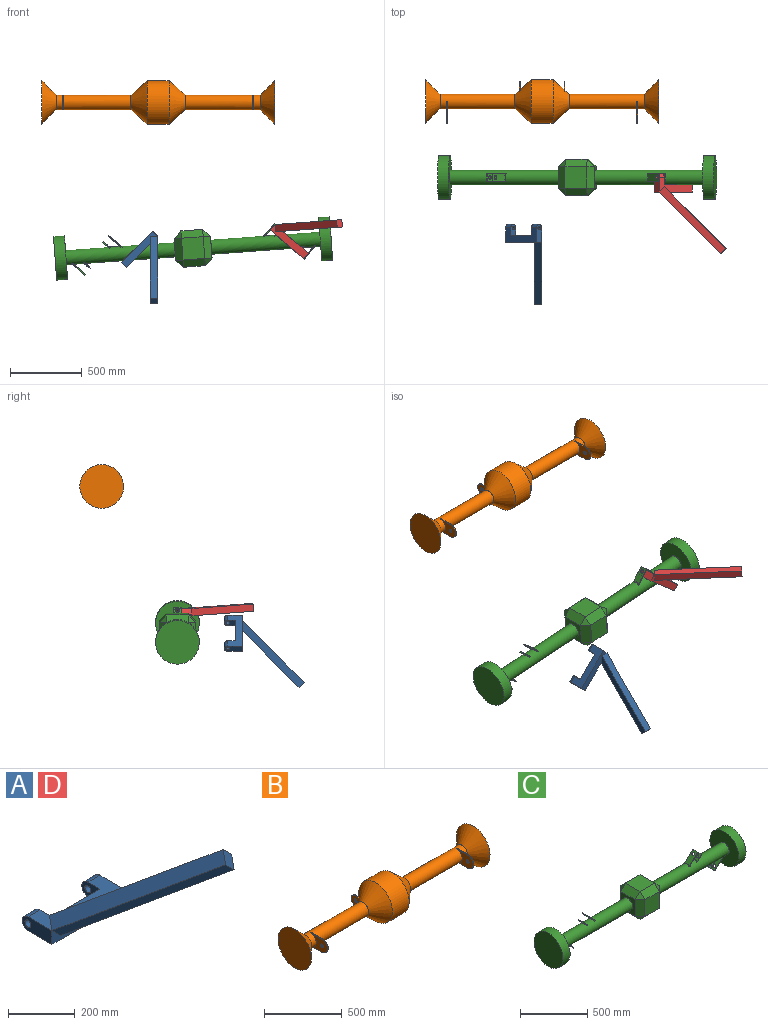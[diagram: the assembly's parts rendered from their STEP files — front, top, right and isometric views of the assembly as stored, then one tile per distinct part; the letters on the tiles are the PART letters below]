
ASSEMBLY  parts=4 mates=1
PART A: 18 faces, bbox 366.1x558.1x381 mm
  f0: plane 76.2x50.8mm, normal (-1,0,0), area 3087.3mm2, adj f2,f3,f4,f5,f6
  f1: plane 127x50.8mm, normal (1,0,0), area 5668mm2, adj f2,f3,f4,f5,f11
  f2: cylinder r=25.4mm len=50.8mm, axis (1,0,0), area 4053.7mm2, adj f0,f1,f3,f4
  f3: plane 304.8x101.6mm, normal (0,0,1), area 19133.4mm2, adj f0,f1,f2,f6,f7,f8,f9,f11
  f4: plane 304.8x101.6mm, normal (0,0,-1), area 20645.1mm2, adj f0,f1,f2,f6,f7,f8,f9,f11
  f5: cylinder r=12.7mm len=50.8mm, axis (1,0,0), area 4053.7mm2, adj f0,f1
  f6: plane 203.2x50.8mm, normal (0,1,0), area 10322.6mm2, adj f0,f3,f4,f7
  f7: plane 76.2x50.8mm, normal (1,0,0), area 3087.3mm2, adj f3,f4,f6,f9,f10
  f8: plane 127x50.8mm, normal (-1,0,0), area 5668mm2, adj f3,f4,f9,f10,f11
  f9: cylinder r=25.4mm len=50.8mm, axis (-1,0,0), area 4053.7mm2, adj f3,f4,f7,f8
  f10: cylinder r=12.7mm len=50.8mm, axis (-1,0,0), area 4053.7mm2, adj f7,f8
  f11: plane 304.8x50.8mm, normal (0,-1,0), area 14193.5mm2, adj f1,f3,f4,f8,f12,f16
  f12: plane 431.05x340.72mm, normal (-0.5,-0.71,-0.5), area 30967.7mm2, adj f11,f15,f16,f17
  f13: plane 50.8x35.92mm, normal (-0.5,0.71,-0.5), area 912.4mm2, adj f3,f14,f17
  f14: plane 431.05x340.72mm, normal (0.5,0.71,0.5), area 30811.1mm2, adj f3,f13,f15,f16,f17
  f15: plane 61.32x61.32mm, normal (0.5,-0.71,0.5), area 2580.6mm2, adj f12,f14,f16,f17
  f16: plane 452.09x330.2mm, normal (0.71,0,-0.71), area 29898.7mm2, adj f3,f11,f12,f14,f15
  f17: plane 466.97x330.2mm, normal (-0.71,0,0.71), area 30967.7mm2, adj f12,f13,f14,f15
PART B: 38 faces, bbox 1625.7x304.9x304.9 mm
  f0: plane 304.8x304.8mm, normal (1,0,0), area 62643.3mm2, adj f1,f15,f16,f17,f18
  f1: cone r=152.4mm half-angle=45deg, axis (1,0,0), area 91723.9mm2, adj f0,f2
  f2: cylinder r=50.8mm len=521.41mm, axis (1,0,0), area 165412.5mm2, adj f1,f3,f26,f29,f30,f31
  f3: cone r=50.8mm half-angle=41.8deg, axis (-1,0,0), area 96611.5mm2, adj f2,f4,f9,f10,f13,f14
  f4: cylinder r=152.4mm len=304.8mm, axis (1,0,0), area 145931.8mm2, adj f3,f5
  f5: cone r=50.8mm half-angle=41.8deg, axis (1,0,0), area 96611.5mm2, adj f4,f6,f20,f21,f24,f25
  f6: cylinder r=50.8mm len=521.41mm, axis (1,0,0), area 165412.5mm2, adj f5,f7,f32,f35,f36,f37
  f7: cone r=152.4mm half-angle=45deg, axis (-1,0,0), area 91723.9mm2, adj f6,f8
  f8: plane 304.8x304.8mm, normal (-1,0,0), area 72965.9mm2, adj f7
  f9: plane 33.01x6.47mm, normal (0,0,1), area 188.4mm2, adj f3,f11,f13,f14
  f10: plane 33.01x6.47mm, normal (0,0,-1), area 188.4mm2, adj f3,f11,f13,f14
  f11: cylinder r=38.1mm len=76.2mm, axis (-1,0,0), area 760.1mm2, adj f9,f10,f13,f14
  f12: cylinder r=12.7mm len=25.4mm, axis (-1,0,0), area 506.7mm2, adj f13,f14
  f13: plane 76.2x70.99mm, normal (1,0,0), area 3772.5mm2, adj f3,f9,f10,f11,f12
  f14: plane 76.2x64.56mm, normal (-1,0,0), area 3322mm2, adj f3,f9,f10,f11,f12
  f15: plane 203.2x6.35mm, normal (0,1,0), area 1290.3mm2, adj f0,f16,f18,f19
  f16: plane 50.8x6.35mm, normal (0,0,1), area 322.6mm2, adj f0,f15,f17,f19
  f17: plane 203.2x6.35mm, normal (0,-1,0), area 1290.3mm2, adj f0,f16,f18,f19
  f18: plane 50.8x6.35mm, normal (0,0,-1), area 322.6mm2, adj f0,f15,f17,f19
  f19: plane 203.2x50.8mm, normal (1,0,0), area 10322.6mm2, adj f15,f16,f17,f18
  f20: plane 33.01x6.47mm, normal (0,0,1), area 188.4mm2, adj f5,f22,f24,f25
  f21: plane 33.01x6.47mm, normal (0,0,-1), area 188.4mm2, adj f5,f22,f24,f25
  f22: cylinder r=38.1mm len=76.2mm, axis (1,0,0), area 760.1mm2, adj f20,f21,f24,f25
  f23: cylinder r=12.7mm len=25.4mm, axis (1,0,0), area 506.7mm2, adj f24,f25
  f24: plane 76.2x70.99mm, normal (-1,0,0), area 3772.5mm2, adj f5,f20,f21,f22,f23
  f25: plane 76.2x64.56mm, normal (1,0,0), area 3322mm2, adj f5,f20,f21,f22,f23
  f26: plane 101.6x6.35mm, normal (0,0,1), area 645.2mm2, adj f2,f27,f30,f31
  f27: cylinder r=50.8mm len=101.6mm, axis (-1,0,0), area 1013.4mm2, adj f26,f29,f30,f31
  f28: cylinder r=12.7mm len=25.4mm, axis (-1,0,0), area 506.7mm2, adj f30,f31
  f29: plane 101.6x6.35mm, normal (0,0,-1), area 645.2mm2, adj f2,f27,f30,f31
  f30: plane 152.4x101.6mm, normal (1,0,0), area 9815.9mm2, adj f2,f26,f27,f28,f29
  f31: plane 152.4x101.6mm, normal (-1,0,0), area 9815.9mm2, adj f2,f26,f27,f28,f29
  f32: plane 101.6x6.35mm, normal (0,0,-1), area 645.2mm2, adj f6,f33,f36,f37
  f33: cylinder r=50.8mm len=101.6mm, axis (1,0,0), area 1013.4mm2, adj f32,f35,f36,f37
  f34: cylinder r=12.7mm len=25.4mm, axis (1,0,0), area 506.7mm2, adj f36,f37
  f35: plane 101.6x6.35mm, normal (0,0,1), area 645.2mm2, adj f6,f33,f36,f37
  f36: plane 152.4x101.6mm, normal (-1,0,0), area 9815.9mm2, adj f6,f32,f33,f34,f35
  f37: plane 152.4x101.6mm, normal (1,0,0), area 9815.9mm2, adj f6,f32,f33,f34,f35
PART C: 82 faces, bbox 1930.4x304.8x304.8 mm
  f0: plane 152.4x152.4mm, normal (0,0,-1), area 23225.8mm2, adj f9,f13,f14,f52
  f1: plane 152.4x152.4mm, normal (0,1,0), area 23225.8mm2, adj f9,f11,f12,f51
  f2: plane 152.4x152.4mm, normal (0,0,1), area 23225.8mm2, adj f11,f17,f20,f55
  f3: plane 152.4x152.4mm, normal (0,-1,0), area 23225.8mm2, adj f14,f18,f20,f56
  f4: plane 152.4x152.4mm, normal (1,0,0), area 15118.4mm2, adj f5,f12,f13,f17,f18
  f5: cylinder r=50.8mm len=762mm, axis (-1,0,0), area 241308.7mm2, adj f4,f8,f21,f22,f23,f25,f26,f27
  f6: cylinder r=152.4mm len=304.8mm, axis (-1,0,0), area 72965.9mm2, adj f7,f8
  f7: plane 304.8x304.8mm, normal (1,0,0), area 72965.9mm2, adj f6
  f8: plane 304.8x304.8mm, normal (-1,0,0), area 64858.6mm2, adj f5,f6
  f9: plane 152.4x50.8mm, normal (0,0.71,-0.71), area 10948.7mm2, adj f0,f1,f10,f50
  f10: plane 50.8x50.8mm, normal (0.58,0.58,-0.58), area 2234.9mm2, adj f9,f12,f13
  f11: plane 152.4x50.8mm, normal (0,0.71,0.71), area 10948.7mm2, adj f1,f2,f15,f53
  f12: plane 152.4x50.8mm, normal (0.71,0.71,0), area 10948.7mm2, adj f1,f4,f10,f15
  f13: plane 152.4x50.8mm, normal (0.71,0,-0.71), area 10948.7mm2, adj f0,f4,f10,f16
  f14: plane 152.4x50.8mm, normal (0,-0.71,-0.71), area 10948.7mm2, adj f0,f3,f16,f54
  f15: plane 50.8x50.8mm, normal (0.58,0.58,0.58), area 2234.9mm2, adj f11,f12,f17
  f16: plane 50.8x50.8mm, normal (0.58,-0.58,-0.58), area 2234.9mm2, adj f13,f14,f18
  f17: plane 152.4x50.8mm, normal (0.71,0,0.71), area 10948.7mm2, adj f2,f4,f15,f19
  f18: plane 152.4x50.8mm, normal (0.71,-0.71,0), area 10948.7mm2, adj f3,f4,f16,f19
  f19: plane 50.8x50.8mm, normal (0.58,-0.58,0.58), area 2234.9mm2, adj f17,f18,f20
  f20: plane 152.4x50.8mm, normal (0,-0.71,0.71), area 10948.7mm2, adj f2,f3,f19,f57
  f21: plane 51.71x47.22mm, normal (0,-1,0), area 403.9mm2, adj f5,f23,f24,f25
  f22: plane 51.71x47.22mm, normal (0,1,0), area 403.9mm2, adj f5,f23,f24,f25
  f23: plane 50.8x42.73mm, normal (-0.71,0,0.71), area 2232.3mm2, adj f5,f21,f22,f24,f44
  f24: plane 50.8x4.49mm, normal (-0.71,0,-0.71), area 322.6mm2, adj f21,f22,f23,f25
  f25: plane 50.8x47.22mm, normal (0.71,0,-0.71), area 2554.9mm2, adj f5,f21,f22,f24,f44
  f26: plane 92.12x87.63mm, normal (0,-1,0), area 766.8mm2, adj f5,f28,f29,f30
  f27: plane 92.12x87.63mm, normal (0,1,0), area 766.8mm2, adj f5,f28,f29,f30
  f28: plane 83.14x83.14mm, normal (-0.71,0,0.71), area 5135.5mm2, adj f5,f26,f27,f29,f43
  f29: plane 50.8x4.49mm, normal (-0.71,0,-0.71), area 322.6mm2, adj f26,f27,f28,f30
  f30: plane 87.63x87.63mm, normal (0.71,0,-0.71), area 5458.1mm2, adj f5,f26,f27,f29,f43
  f31: plane 92.12x87.63mm, normal (0,-1,0), area 766.8mm2, adj f5,f33,f34,f35
  f32: plane 92.12x87.63mm, normal (0,1,0), area 766.8mm2, adj f5,f33,f34,f35
  f33: plane 87.63x87.63mm, normal (-0.71,0,0.71), area 5458.1mm2, adj f5,f31,f32,f35,f42
  f34: plane 83.14x83.14mm, normal (0.71,0,-0.71), area 5135.5mm2, adj f5,f31,f32,f35,f42
  f35: plane 50.8x4.49mm, normal (0.71,0,0.71), area 322.6mm2, adj f31,f32,f33,f34
  f36: plane 51.71x47.22mm, normal (0,-1,0), area 403.9mm2, adj f5,f38,f39,f40
  f37: plane 51.71x47.22mm, normal (0,1,0), area 403.9mm2, adj f5,f38,f39,f40
  f38: plane 50.8x42.73mm, normal (0.71,0,-0.71), area 2232.3mm2, adj f5,f36,f37,f39,f41
  f39: plane 50.8x4.49mm, normal (0.71,0,0.71), area 322.6mm2, adj f36,f37,f38,f40
  f40: plane 50.8x47.22mm, normal (-0.71,0,0.71), area 2554.9mm2, adj f5,f36,f37,f39,f41
  f41: cylinder r=12.7mm len=25.4mm, axis (-0.71,0,0.71), area 506.7mm2, adj f38,f40
  f42: cylinder r=12.7mm len=25.4mm, axis (-0.71,0,0.71), area 506.7mm2, adj f33,f34
  f43: cylinder r=12.7mm len=25.4mm, axis (0.71,0,-0.71), area 506.7mm2, adj f28,f30
  f44: cylinder r=12.7mm len=25.4mm, axis (0.71,0,-0.71), area 506.7mm2, adj f23,f25
  f45: plane 152.4x152.4mm, normal (-1,0,0), area 15118.4mm2, adj f46,f51,f52,f55,f56
  f46: cylinder r=50.8mm len=762mm, axis (1,0,0), area 241308.7mm2, adj f45,f49,f58,f59,f60,f62,f63,f64
  f47: cylinder r=152.4mm len=304.8mm, axis (1,0,0), area 72965.9mm2, adj f48,f49
  f48: plane 304.8x304.8mm, normal (-1,0,0), area 72965.9mm2, adj f47
  f49: plane 304.8x304.8mm, normal (1,0,0), area 64858.6mm2, adj f46,f47
  f50: plane 50.8x50.8mm, normal (-0.58,0.58,-0.58), area 2234.9mm2, adj f9,f51,f52
  f51: plane 152.4x50.8mm, normal (-0.71,0.71,0), area 10948.7mm2, adj f1,f45,f50,f53
  f52: plane 152.4x50.8mm, normal (-0.71,0,-0.71), area 10948.7mm2, adj f0,f45,f50,f54
  f53: plane 50.8x50.8mm, normal (-0.58,0.58,0.58), area 2234.9mm2, adj f11,f51,f55
  f54: plane 50.8x50.8mm, normal (-0.58,-0.58,-0.58), area 2234.9mm2, adj f14,f52,f56
  f55: plane 152.4x50.8mm, normal (-0.71,0,0.71), area 10948.7mm2, adj f2,f45,f53,f57
  f56: plane 152.4x50.8mm, normal (-0.71,-0.71,0), area 10948.7mm2, adj f3,f45,f54,f57
  f57: plane 50.8x50.8mm, normal (-0.58,-0.58,0.58), area 2234.9mm2, adj f20,f55,f56
  f58: plane 51.71x47.22mm, normal (0,-1,0), area 403.9mm2, adj f46,f60,f61,f62
  f59: plane 51.71x47.22mm, normal (0,1,0), area 403.9mm2, adj f46,f60,f61,f62
  f60: plane 50.8x42.73mm, normal (0.71,0,0.71), area 2232.3mm2, adj f46,f58,f59,f61,f81
  f61: plane 50.8x4.49mm, normal (0.71,0,-0.71), area 322.6mm2, adj f58,f59,f60,f62
  f62: plane 50.8x47.22mm, normal (-0.71,0,-0.71), area 2554.9mm2, adj f46,f58,f59,f61,f81
  f63: plane 92.12x87.63mm, normal (0,-1,0), area 766.8mm2, adj f46,f65,f66,f67
  f64: plane 92.12x87.63mm, normal (0,1,0), area 766.8mm2, adj f46,f65,f66,f67
  f65: plane 83.14x83.14mm, normal (0.71,0,0.71), area 5135.5mm2, adj f46,f63,f64,f66,f80
  f66: plane 50.8x4.49mm, normal (0.71,0,-0.71), area 322.6mm2, adj f63,f64,f65,f67
  f67: plane 87.63x87.63mm, normal (-0.71,0,-0.71), area 5458.1mm2, adj f46,f63,f64,f66,f80
  f68: plane 92.12x87.63mm, normal (0,-1,0), area 766.8mm2, adj f46,f70,f71,f72
  f69: plane 92.12x87.63mm, normal (0,1,0), area 766.8mm2, adj f46,f70,f71,f72
  f70: plane 87.63x87.63mm, normal (0.71,0,0.71), area 5458.1mm2, adj f46,f68,f69,f72,f79
  f71: plane 83.14x83.14mm, normal (-0.71,0,-0.71), area 5135.5mm2, adj f46,f68,f69,f72,f79
  f72: plane 50.8x4.49mm, normal (-0.71,0,0.71), area 322.6mm2, adj f68,f69,f70,f71
  f73: plane 51.71x47.22mm, normal (0,-1,0), area 403.9mm2, adj f46,f75,f76,f77
  f74: plane 51.71x47.22mm, normal (0,1,0), area 403.9mm2, adj f46,f75,f76,f77
  f75: plane 50.8x42.73mm, normal (-0.71,0,-0.71), area 2232.3mm2, adj f46,f73,f74,f76,f78
  f76: plane 50.8x4.49mm, normal (-0.71,0,0.71), area 322.6mm2, adj f73,f74,f75,f77
  f77: plane 50.8x47.22mm, normal (0.71,0,0.71), area 2554.9mm2, adj f46,f73,f74,f76,f78
  f78: cylinder r=12.7mm len=25.4mm, axis (0.71,0,0.71), area 506.7mm2, adj f75,f77
  f79: cylinder r=12.7mm len=25.4mm, axis (0.71,0,0.71), area 506.7mm2, adj f70,f71
  f80: cylinder r=12.7mm len=25.4mm, axis (-0.71,0,-0.71), area 506.7mm2, adj f65,f67
  f81: cylinder r=12.7mm len=25.4mm, axis (-0.71,0,-0.71), area 506.7mm2, adj f60,f62
PART D: same geometry as A
PLACE A rot(axis=(0,1,0),135.3deg) t=(-51.58,-478.26,-581.22)mm
PLACE B t=(77.4,401.55,443.21)mm
PLACE C rot(axis=(0,-1,0),4.1deg) t=(321.14,-126.82,-574.7)mm
PLACE D rot(axis=(0,1,0),40.9deg) t=(991.55,-126.82,-527.49)mm
MATE revolute D.f5 <-> C.f43  axis (0.76,0,-0.65) through (1087.61,-126.82,-610.57)mm
